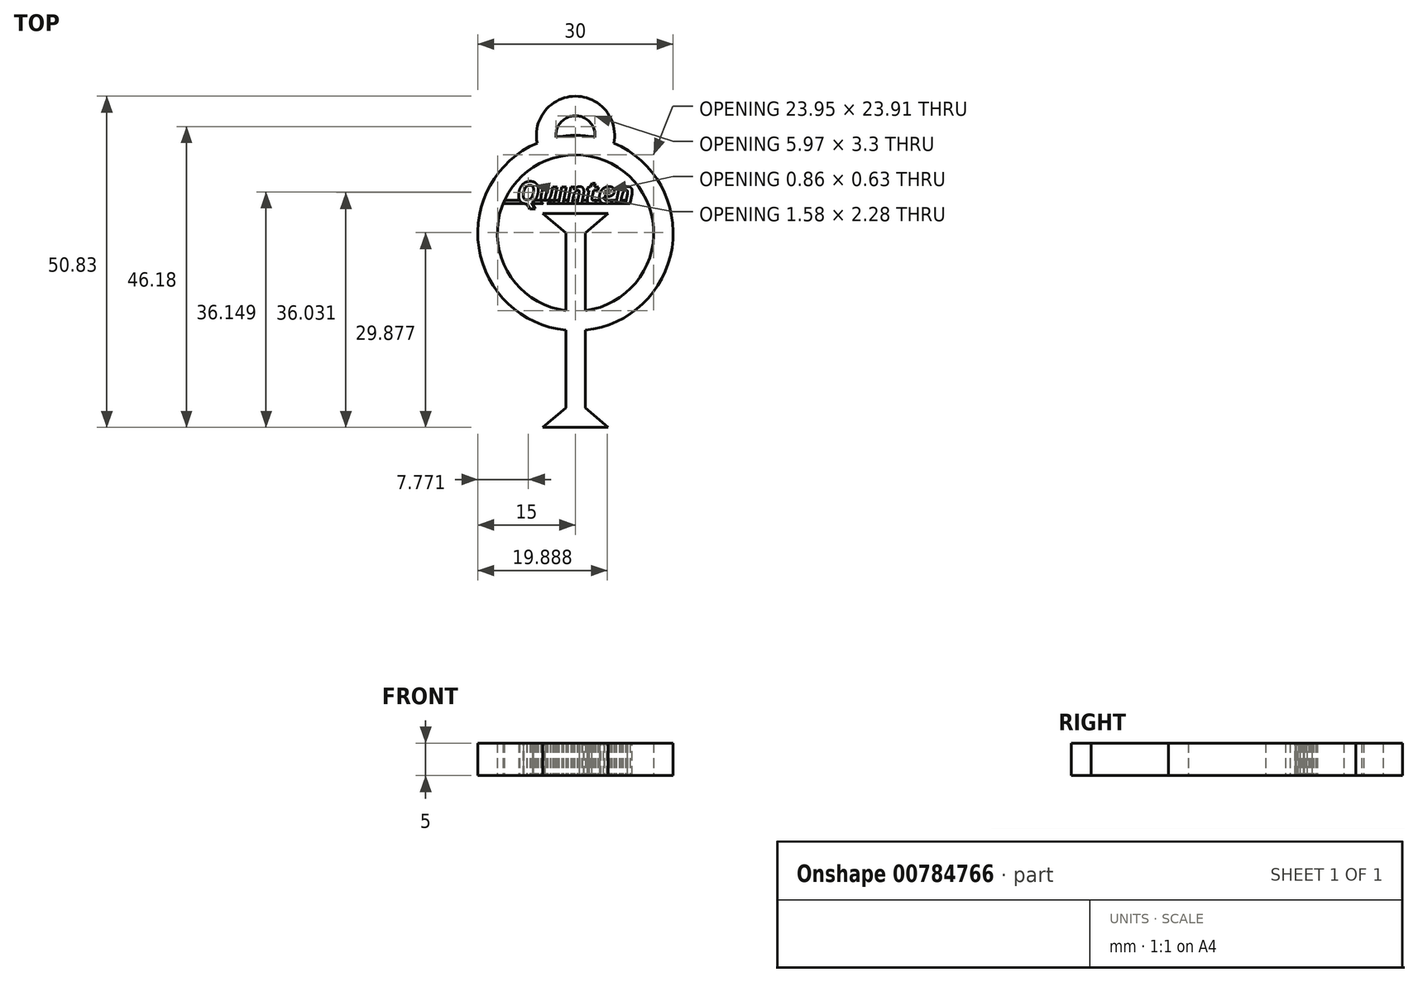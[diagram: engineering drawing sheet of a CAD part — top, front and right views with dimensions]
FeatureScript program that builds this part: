
annotation { "Feature Type Name" : "Feature", "Feature Type Description" : "" }
export const myFeature = defineFeature(function(context is Context, id is Id, definition is map)
    precondition{}
    {
        {
            var Q0;
            Q0=qCreatedBy(makeId("Top.planeOp"),FACE);
            var sketch = newSketch(context, id + "F0", { "sketchPlane" : qUnion([Q0])});
            skCircle(sketch, "E0", {"center": v(0, 0) * mm, "radius": 15 * mm});
            skCircle(sketch, "E1", {"center": v(0, 0) * mm, "radius": 12 * mm});
            skLineSegment(sketch, "E2", {"start": v(0, 0) * mm, "end": v(0, 0) * mm});
            skLineSegment(sketch, "E3", {"start": v(-1.5, 0) * mm, "end": v(-1.5, -11.9) * mm});
            skLineSegment(sketch, "E4", {"start": v(1.5, 0) * mm, "end": v(1.5, -11.9) * mm});
            skLineSegment(sketch, "E5", {"start": v(1.5, -13.42) * mm, "end": v(-1.5, -13.42) * mm, "construction": true});
            skLineSegment(sketch, "E6.MirrorCS", {"start": v(1.5, -26.83) * mm, "end": v(1.5, -14.92) * mm});
            skLineSegment(sketch, "E7.MirrorCS", {"start": v(-1.5, -26.83) * mm, "end": v(-1.5, -14.92) * mm});
            skLineSegment(sketch, "E8.MirrorCS", {"start": v(-1.5, -26.83) * mm, "end": v(1.5, -26.83) * mm});
            skLineSegment(sketch, "E9", {"start": v(0, 0) * mm, "end": v(0, 3) * mm});
            skLineSegment(sketch, "E10", {"start": v(0, 3) * mm, "end": v(-5, 3) * mm, "construction": true});
            skLineSegment(sketch, "E11", {"start": v(-5, 3) * mm, "end": v(5, 3) * mm});
            skLineSegment(sketch, "E12", {"start": v(5, 3) * mm, "end": v(1.5, 0) * mm});
            skLineSegment(sketch, "E13", {"start": v(-5, 3) * mm, "end": v(-1.5, 0) * mm});
            skLineSegment(sketch, "E14.MirrorCS", {"start": v(-5, -29.83) * mm, "end": v(5, -29.83) * mm});
            skLineSegment(sketch, "E15.MirrorCS", {"start": v(5, -29.83) * mm, "end": v(1.5, -26.83) * mm});
            skLineSegment(sketch, "E16.MirrorCS", {"start": v(-5, -29.83) * mm, "end": v(-1.5, -26.83) * mm});
            skText(sketch, "E17", { "text": "Quinten", "fontName": "OpenSans-BoldItalic.ttf"});
            skLineSegment(sketch, "E18.bottom", {"start": v(-9.02, 4.51) * mm, "end": v(9.02, 4.51) * mm});
            skLineSegment(sketch, "E18.top", {"start": v(-9.02, 5.01) * mm, "end": v(9.02, 5.01) * mm});
            skLineSegment(sketch, "E18.left", {"start": v(-9.02, 4.51) * mm, "end": v(-9.02, 5.01) * mm});
            skLineSegment(sketch, "E18.right", {"start": v(9.02, 4.51) * mm, "end": v(9.02, 5.01) * mm});
            skLineSegment(sketch, "E19", {"start": v(-1.5, -11.9) * mm, "end": v(-1.5, -13.42) * mm, "construction": true});
            skLineSegment(sketch, "E20", {"start": v(-1.5, -14.92) * mm, "end": v(-1.5, -13.42) * mm, "construction": true});
            skLineSegment(sketch, "E21", {"start": v(1.5, -14.92) * mm, "end": v(1.5, -13.42) * mm, "construction": true});
            skLineSegment(sketch, "E22", {"start": v(1.5, -11.9) * mm, "end": v(1.5, -13.42) * mm, "construction": true});
            skLineSegment(sketch, "E23", {"start": v(-9.02, 5.01) * mm, "end": v(-11.36, 5.01) * mm});
            skLineSegment(sketch, "E24", {"start": v(-11.36, 5.01) * mm, "end": v(-11.36, 4.51) * mm});
            skLineSegment(sketch, "E25", {"start": v(-11.36, 4.51) * mm, "end": v(-9.02, 4.51) * mm});
            skLineSegment(sketch, "E26.bottom", {"start": v(9.02, 5.01) * mm, "end": v(11.41, 5.01) * mm});
            skLineSegment(sketch, "E26.top", {"start": v(9.02, 4.51) * mm, "end": v(11.41, 4.51) * mm});
            skLineSegment(sketch, "E26.left", {"start": v(9.02, 5.01) * mm, "end": v(9.02, 4.51) * mm});
            skLineSegment(sketch, "E26.right", {"start": v(11.41, 5.01) * mm, "end": v(11.41, 4.51) * mm});
            skArc(sketch, "E27", {"start": v(2.98, 14.7) * mm, "mid": v(0, 18) * mm, "end": v(-2.98, 14.7) * mm});
            skArc(sketch, "E28", {"start": v(5.88, 13.8) * mm, "mid": v(0, 21) * mm, "end": v(-5.88, 13.8) * mm});
            const initialGuessF0  = {"E17": [-0.00902, 0.00451, 1, 0, 0.0034]};
            skSetInitialGuess(sketch, initialGuessF0);
            skSolve(sketch);
        }
        {
            var Q0;
            Q0=qSketchRegion(id+"F0",true);
            var Q1;
            {var subQ0=sQuery(id+"F0.wireOp",EDGE,"E12");Q1=makeQuery(id+"F0.imprint","IMPRINT",FACE,{"disambiguationData":[TD([[makeQuery(id+"F0.imprint","IMPRINT",EDGE,{"derivedFrom":subQ0}),-1.0]])]});}
            var Q2;
            {var subQ0=sQuery(id+"F0.wireOp",EDGE,"E17.sketch_text.stroke-0");Q2=makeQuery(id+"F0.imprint","IMPRINT",FACE,{"disambiguationData":[TD([[makeQuery(id+"F0.imprint","IMPRINT",EDGE,{"derivedFrom":subQ0}),-1.0]])]});}
            var Q3;
            {var subQ7=sQuery(id+"F0.wireOp",EDGE,"E17.sketch_text.stroke-2");var subQ8=sQuery(id+"F0.wireOp",EDGE,"E17.sketch_text.stroke-1");var subQ9=makeQuery(id+"F0.imprint","INTERSECT",VERTEX,{"derivedFrom":[subQ8,subQ7]});Q3=makeQuery(id+"F0.imprint","IMPRINT",FACE,{"disambiguationData":[TD([[makeQuery(id+"F0.imprint","IMPRINT",EDGE,{"disambiguationData":[TD([[subQ9,1.0]])],"derivedFrom":subQ8}),-1.0]])]});}
            var Q4;
            {var subQ1=sQuery(id+"F0.wireOp",EDGE,"E17.sketch_text.stroke-3");Q4=makeQuery(id+"F0.imprint","IMPRINT",FACE,{"disambiguationData":[TD([[makeQuery(id+"F0.imprint","IMPRINT",EDGE,{"derivedFrom":subQ1}),-1.0]])]});}
            var Q5;
            Q5=makeQuery(id+"F0.imprint","IMPRINT",FACE,{"disambiguationData":[TD([[makeQuery(id+"F0.imprint","IMPRINT",EDGE,{"derivedFrom":sQuery(id+"F0.wireOp",EDGE,"E17.sketch_text.stroke-23")}),-1.0]])]});
            var Q6;
            {var subQ4=sQuery(id+"F0.wireOp",EDGE,"E17.sketch_text.stroke-33");Q6=makeQuery(id+"F0.imprint","IMPRINT",FACE,{"disambiguationData":[TD([[makeQuery(id+"F0.imprint","IMPRINT",EDGE,{"derivedFrom":subQ4}),-1.0]])]});}
            var Q7;
            {var subQ0=sQuery(id+"F0.wireOp",EDGE,"E17.sketch_text.stroke-49");Q7=makeQuery(id+"F0.imprint","IMPRINT",FACE,{"disambiguationData":[TD([[makeQuery(id+"F0.imprint","IMPRINT",EDGE,{"derivedFrom":subQ0}),-1.0]])]});}
            var Q8;
            {var subQ0=sQuery(id+"F0.wireOp",EDGE,"E18.bottom");var subQ1=sQuery(id+"F0.wireOp",EDGE,"E17.sketch_text.stroke-48");var subQ2=makeQuery(id+"F0.imprint","INTERSECT",VERTEX,{"derivedFrom":[subQ1,subQ0]});Q8=makeQuery(id+"F0.imprint","IMPRINT",FACE,{"disambiguationData":[TD([[makeQuery(id+"F0.imprint","IMPRINT",EDGE,{"disambiguationData":[TD([[subQ2,-1.0]])],"derivedFrom":subQ1}),-1.0]])]});}
            var Q9;
            {var subQ11=sQuery(id+"F0.wireOp",EDGE,"E17.sketch_text.stroke-53");Q9=makeQuery(id+"F0.imprint","IMPRINT",FACE,{"disambiguationData":[TD([[makeQuery(id+"F0.imprint","IMPRINT",EDGE,{"derivedFrom":subQ11}),-1.0]])]});}
            var Q10;
            {var subQ0=sQuery(id+"F0.wireOp",EDGE,"E18.bottom");var subQ1=sQuery(id+"F0.wireOp",EDGE,"E17.sketch_text.stroke-57");var subQ2=makeQuery(id+"F0.imprint","INTERSECT",VERTEX,{"derivedFrom":[subQ1,subQ0]});Q10=makeQuery(id+"F0.imprint","IMPRINT",FACE,{"disambiguationData":[TD([[makeQuery(id+"F0.imprint","IMPRINT",EDGE,{"disambiguationData":[TD([[subQ2,1.0]])],"derivedFrom":subQ1}),-1.0]])]});}
            var Q11;
            {var subQ0=sQuery(id+"F0.wireOp",EDGE,"E18.bottom");var subQ1=sQuery(id+"F0.wireOp",EDGE,"E17.sketch_text.stroke-52");var subQ2=makeQuery(id+"F0.imprint","INTERSECT",VERTEX,{"derivedFrom":[subQ1,subQ0]});Q11=makeQuery(id+"F0.imprint","IMPRINT",FACE,{"disambiguationData":[TD([[makeQuery(id+"F0.imprint","IMPRINT",EDGE,{"disambiguationData":[TD([[subQ2,-1.0]])],"derivedFrom":subQ1}),-1.0]])]});}
            var Q12;
            {var subQ0=sQuery(id+"F0.wireOp",EDGE,"E17.sketch_text.stroke-68");Q12=makeQuery(id+"F0.imprint","IMPRINT",FACE,{"disambiguationData":[TD([[makeQuery(id+"F0.imprint","IMPRINT",EDGE,{"derivedFrom":subQ0}),-1.0]])]});}
            var Q13;
            {var subQ5=sQuery(id+"F0.wireOp",EDGE,"E17.sketch_text.stroke-70");var subQ6=sQuery(id+"F0.wireOp",EDGE,"E17.sketch_text.stroke-69");var subQ7=makeQuery(id+"F0.imprint","INTERSECT",VERTEX,{"derivedFrom":[subQ6,subQ5]});Q13=makeQuery(id+"F0.imprint","IMPRINT",FACE,{"disambiguationData":[TD([[makeQuery(id+"F0.imprint","IMPRINT",EDGE,{"disambiguationData":[TD([[subQ7,1.0]])],"derivedFrom":subQ6}),-1.0]])]});}
            var Q14;
            Q14=makeQuery(id+"F0.imprint","IMPRINT",FACE,{"disambiguationData":[TD([[makeQuery(id+"F0.imprint","IMPRINT",EDGE,{"derivedFrom":sQuery(id+"F0.wireOp",EDGE,"E17.sketch_text.stroke-87")}),-1.0]])]});
            var Q15;
            {var subQ5=sQuery(id+"F0.wireOp",EDGE,"E17.sketch_text.stroke-94");var subQ6=sQuery(id+"F0.wireOp",EDGE,"E17.sketch_text.stroke-93");var subQ7=makeQuery(id+"F0.imprint","INTERSECT",VERTEX,{"derivedFrom":[subQ6,subQ5]});Q15=makeQuery(id+"F0.imprint","IMPRINT",FACE,{"disambiguationData":[TD([[makeQuery(id+"F0.imprint","IMPRINT",EDGE,{"disambiguationData":[TD([[subQ7,1.0]])],"derivedFrom":subQ6}),-1.0]])]});}
            var Q16;
            {var subQ7=sQuery(id+"F0.wireOp",EDGE,"E17.sketch_text.stroke-113");Q16=makeQuery(id+"F0.imprint","IMPRINT",FACE,{"disambiguationData":[TD([[makeQuery(id+"F0.imprint","IMPRINT",EDGE,{"derivedFrom":subQ7}),-1.0]])]});}
            var Q17;
            {var subQ0=sQuery(id+"F0.wireOp",EDGE,"E18.bottom");var subQ1=sQuery(id+"F0.wireOp",EDGE,"E17.sketch_text.stroke-112");var subQ2=makeQuery(id+"F0.imprint","INTERSECT",VERTEX,{"derivedFrom":[subQ1,subQ0]});Q17=makeQuery(id+"F0.imprint","IMPRINT",FACE,{"disambiguationData":[TD([[makeQuery(id+"F0.imprint","IMPRINT",EDGE,{"disambiguationData":[TD([[subQ2,-1.0]])],"derivedFrom":subQ1}),-1.0]])]});}
            var Q18;
            {var subQ0=sQuery(id+"F0.wireOp",EDGE,"E18.bottom");var subQ1=sQuery(id+"F0.wireOp",EDGE,"E17.sketch_text.stroke-117");var subQ2=makeQuery(id+"F0.imprint","INTERSECT",VERTEX,{"derivedFrom":[subQ1,subQ0]});Q18=makeQuery(id+"F0.imprint","IMPRINT",FACE,{"disambiguationData":[TD([[makeQuery(id+"F0.imprint","IMPRINT",EDGE,{"disambiguationData":[TD([[subQ2,1.0]])],"derivedFrom":subQ1}),-1.0]])]});}
            var Q19;
            {var subQ5=sQuery(id+"F0.wireOp",EDGE,"E26.right");Q19=makeQuery(id+"F0.imprint","IMPRINT",FACE,{"disambiguationData":[TD([[makeQuery(id+"F0.imprint","IMPRINT",EDGE,{"derivedFrom":subQ5}),-1.0]])]});}
            var Q20;
            {var subQ5=sQuery(id+"F0.wireOp",EDGE,"E24");Q20=makeQuery(id+"F0.imprint","IMPRINT",FACE,{"disambiguationData":[TD([[makeQuery(id+"F0.imprint","IMPRINT",EDGE,{"derivedFrom":subQ5}),1.0]])]});}
            extrude(context, id + "F1", {"entities" : qUnion([Q0, Q1, Q2, Q3, Q4, Q5, Q6, Q7, Q8, Q9, Q10, Q11, Q12, Q13, Q14, Q15, Q16, Q17, Q18, Q19, Q20]), "depth" : 5 * mm, "offsetDistance" : 25 * mm});
        }
        {
            var Q0;
            {var subQ0=sQuery(id+"F0.wireOp",EDGE,"E18.bottom");var subQ1=sQuery(id+"F0.wireOp",EDGE,"E17.sketch_text.stroke-50");var subQ2=makeQuery(id+"F0.imprint","INTERSECT",VERTEX,{"derivedFrom":[subQ1,subQ0]});Q0=makeQuery(id+"F0.imprint","IMPRINT",FACE,{"disambiguationData":[TD([[makeQuery(id+"F0.imprint","IMPRINT",EDGE,{"disambiguationData":[TD([[subQ2,1.0]])],"derivedFrom":subQ1}),1.0]])]});}
            var Q1;
            {var subQ0=sQuery(id+"F0.wireOp",EDGE,"E18.bottom");var subQ1=sQuery(id+"F0.wireOp",EDGE,"E17.sketch_text.stroke-52");var subQ2=makeQuery(id+"F0.imprint","INTERSECT",VERTEX,{"derivedFrom":[subQ1,subQ0]});Q1=makeQuery(id+"F0.imprint","IMPRINT",FACE,{"disambiguationData":[TD([[makeQuery(id+"F0.imprint","IMPRINT",EDGE,{"disambiguationData":[TD([[subQ2,-1.0]])],"derivedFrom":subQ1}),1.0]])]});}
            var Q2;
            {var subQ5=sQuery(id+"F0.wireOp",EDGE,"E18.bottom");var subQ6=sQuery(id+"F0.wireOp",EDGE,"E17.sketch_text.stroke-67");var subQ7=makeQuery(id+"F0.imprint","INTERSECT",VERTEX,{"derivedFrom":[subQ6,subQ5]});Q2=makeQuery(id+"F0.imprint","IMPRINT",FACE,{"disambiguationData":[TD([[makeQuery(id+"F0.imprint","IMPRINT",EDGE,{"disambiguationData":[TD([[subQ7,1.0]])],"derivedFrom":subQ6}),1.0]])]});}
            var Q3;
            {var subQ6=sQuery(id+"F0.wireOp",EDGE,"E17.sketch_text.stroke-70");var subQ9=sQuery(id+"F0.wireOp",EDGE,"E17.sketch_text.stroke-69");var subQ10=makeQuery(id+"F0.imprint","INTERSECT",VERTEX,{"derivedFrom":[subQ9,subQ6]});Q3=makeQuery(id+"F0.imprint","IMPRINT",FACE,{"disambiguationData":[TD([[makeQuery(id+"F0.imprint","IMPRINT",EDGE,{"disambiguationData":[TD([[subQ10,1.0]])],"derivedFrom":subQ9}),1.0]])]});}
            var Q4;
            {var subQ3=sQuery(id+"F0.wireOp",EDGE,"E17.sketch_text.stroke-110");var subQ7=sQuery(id+"F0.wireOp",EDGE,"E17.sketch_text.stroke-109");var subQ8=makeQuery(id+"F0.imprint","INTERSECT",VERTEX,{"derivedFrom":[subQ7,subQ3]});Q4=makeQuery(id+"F0.imprint","IMPRINT",FACE,{"disambiguationData":[TD([[makeQuery(id+"F0.imprint","IMPRINT",EDGE,{"disambiguationData":[TD([[subQ8,1.0]])],"derivedFrom":subQ7}),1.0]])]});}
            var Q5;
            {var subQ0=sQuery(id+"F0.wireOp",EDGE,"E18.bottom");var subQ1=sQuery(id+"F0.wireOp",EDGE,"E17.sketch_text.stroke-112");var subQ2=makeQuery(id+"F0.imprint","INTERSECT",VERTEX,{"derivedFrom":[subQ1,subQ0]});Q5=makeQuery(id+"F0.imprint","IMPRINT",FACE,{"disambiguationData":[TD([[makeQuery(id+"F0.imprint","IMPRINT",EDGE,{"disambiguationData":[TD([[subQ2,-1.0]])],"derivedFrom":subQ1}),1.0]])]});}
            var Q6;
            {var subQ5=sQuery(id+"F0.wireOp",EDGE,"E26.left");Q6=makeQuery(id+"F0.imprint","IMPRINT",FACE,{"disambiguationData":[TD([[makeQuery(id+"F0.imprint","IMPRINT",EDGE,{"derivedFrom":subQ5}),-1.0]])]});}
            var Q7;
            {var subQ5=sQuery(id+"F0.wireOp",EDGE,"E26.left");Q7=makeQuery(id+"F0.imprint","IMPRINT",FACE,{"disambiguationData":[TD([[makeQuery(id+"F0.imprint","IMPRINT",EDGE,{"derivedFrom":subQ5}),1.0]])]});}
            var Q8;
            {var subQ5=sQuery(id+"F0.wireOp",EDGE,"E18.left");Q8=makeQuery(id+"F0.imprint","IMPRINT",FACE,{"disambiguationData":[TD([[makeQuery(id+"F0.imprint","IMPRINT",EDGE,{"derivedFrom":subQ5}),1.0]])]});}
            var Q9;
            {var subQ0=sQuery(id+"F0.wireOp",EDGE,"E18.left");Q9=makeQuery(id+"F0.imprint","IMPRINT",FACE,{"disambiguationData":[TD([[makeQuery(id+"F0.imprint","IMPRINT",EDGE,{"derivedFrom":subQ0}),-1.0]])]});}
            var Q10;
            {var subQ5=sQuery(id+"F0.wireOp",EDGE,"E17.sketch_text.stroke-2");var subQ6=sQuery(id+"F0.wireOp",EDGE,"E17.sketch_text.stroke-1");var subQ7=makeQuery(id+"F0.imprint","INTERSECT",VERTEX,{"derivedFrom":[subQ6,subQ5]});Q10=makeQuery(id+"F0.imprint","IMPRINT",FACE,{"disambiguationData":[TD([[makeQuery(id+"F0.imprint","IMPRINT",EDGE,{"disambiguationData":[TD([[subQ7,1.0]])],"derivedFrom":subQ6}),1.0]])]});}
            var Q11;
            {var subQ0=sQuery(id+"F0.wireOp",EDGE,"E18.bottom");var subQ1=sQuery(id+"F0.wireOp",EDGE,"E17.sketch_text.stroke-31");var subQ2=makeQuery(id+"F0.imprint","INTERSECT",VERTEX,{"derivedFrom":[subQ1,subQ0]});Q11=makeQuery(id+"F0.imprint","IMPRINT",FACE,{"disambiguationData":[TD([[makeQuery(id+"F0.imprint","IMPRINT",EDGE,{"disambiguationData":[TD([[subQ2,1.0]])],"derivedFrom":subQ1}),1.0]])]});}
            var Q12;
            {var subQ0=sQuery(id+"F0.wireOp",EDGE,"E17.sketch_text.stroke-33");Q12=makeQuery(id+"F0.imprint","IMPRINT",FACE,{"disambiguationData":[TD([[makeQuery(id+"F0.imprint","IMPRINT",EDGE,{"derivedFrom":subQ0}),1.0]])]});}
            extrude(context, id + "F2", {"entities" : qUnion([Q0, Q1, Q2, Q3, Q4, Q5, Q6, Q7, Q8, Q9, Q10, Q11, Q12]), "depth" : 5 * mm, "offsetDistance" : 25 * mm});
        }
    });
